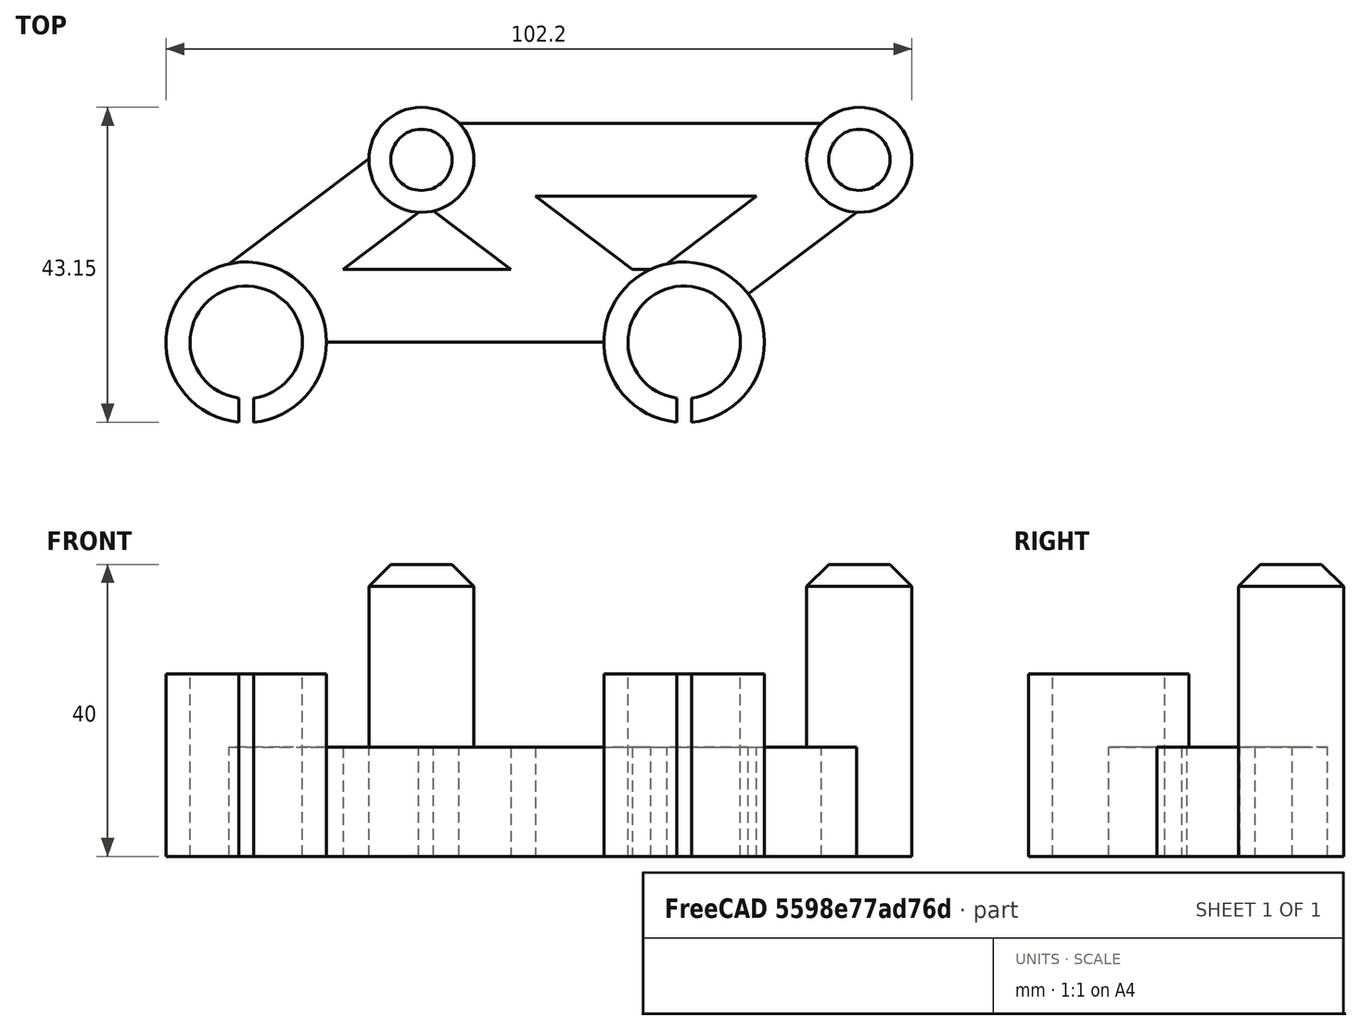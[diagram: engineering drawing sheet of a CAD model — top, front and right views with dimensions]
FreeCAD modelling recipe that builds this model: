
FCSTD DOCUMENT  (FreeCAD 0.17R13541 (Git))
Label: offset-rod-adaptor
License: All rights reserved
LicenseURL: http://en.wikipedia.org/wiki/All_rights_reserved
objects: Part::Box×7, Part::Cylinder×6, Part::Fuse×5, Part::Cut×4, Part::MultiFuse×2, Part::Chamfer×1
note: 25 computed .brp shape members not serialized (recipe doc carries the construction recipe); baked Part::Feature solids carry a one-line shape summary decoded from their .brp

FEATURE [Part::Cylinder] Cylinder
  Angle = 360
  AttacherType = Attacher::AttachEngine3D
  Height = 25
  Radius = 7.7
FEATURE [Part::Cylinder] Cylinder001
  Angle = 360
  AttacherType = Attacher::AttachEngine3D
  Height = 25
  Placement = pos=(60,0,0) rot=(0,0,1;0rad)
  Radius = 7.7
FEATURE [Part::Cylinder] Cylinder002
  Angle = 360
  AttacherType = Attacher::AttachEngine3D
  Height = 25
  Radius = 11
FEATURE [Part::Cylinder] Cylinder003
  Angle = 360
  AttacherType = Attacher::AttachEngine3D
  Height = 25
  Placement = pos=(60,0,0) rot=(0,0,1;0rad)
  Radius = 11
FEATURE [Part::Box] Box  label="Cube"
  AttacherType = Attacher::AttachEngine3D
  Height = 15
  Length = 60
  Width = 10
FEATURE [Part::MultiFuse] Fusion
  Shapes = -> [Cylinder003,Box,Cylinder002]
FEATURE [Part::Cylinder] Cylinder004
  Angle = 360
  AttacherType = Attacher::AttachEngine3D
  Height = 40
  Radius = 7.2
FEATURE [Part::Cylinder] Cylinder005
  Angle = 360
  AttacherType = Attacher::AttachEngine3D
  Height = 40
  Placement = pos=(60,0,0) rot=(0,0,1;0rad)
  Radius = 7.2
FEATURE [Part::Box] Box001  label="Cube001"
  AttacherType = Attacher::AttachEngine3D
  Height = 15
  Length = 60
  Placement = pos=(0,-5,0) rot=(0,0,1;0rad)
  Width = 10
FEATURE [Part::Fuse] Fusion001
  Base = -> Cylinder004
  Tool = -> Cylinder005
FEATURE [Part::Fuse] Fusion002
  Base = -> Box001
  Tool = -> Fusion001
FEATURE [Part::Chamfer] Chamfer
  Base = -> Fusion002
  Edges = 2 edges r=3: [Edge1,Edge21]
  Placement = pos=(24,25,0) rot=(0,0,1;0rad)
FEATURE [Part::Box] Box002  label="Cube002"
  AttacherType = Attacher::AttachEngine3D
  Height = 15
  Length = 34
  Placement = pos=(0,0,0) rot=(0,0,1;0.645772rad)
  Width = 10
FEATURE [Part::Box] Box003  label="Cube003"
  AttacherType = Attacher::AttachEngine3D
  Height = 15
  Length = 34
  Placement = pos=(60,0,0) rot=(0,0,1;0.645772rad)
  Width = 10
FEATURE [Part::Box] Box004  label="Cube004"
  AttacherType = Attacher::AttachEngine3D
  Height = 15
  Length = 32
  Placement = pos=(23,20,0) rot=(0,0,-1;0.645772rad)
  Width = 10
FEATURE [Part::Fuse] Fusion003
  Base = -> Fusion
  Tool = -> Box004
FEATURE [Part::Fuse] Fusion004
  Base = -> Box003
  Tool = -> Fusion003
FEATURE [Part::Fuse] Fusion005
  Base = -> Box002
  Tool = -> Fusion004
FEATURE [Part::Cut] Cut
  Base = -> Fusion005
  Tool = -> Cylinder
FEATURE [Part::Cut] Cut001
  Base = -> Cut
  Tool = -> Cylinder001
FEATURE [Part::Box] Box005  label="Cube005"
  AttacherType = Attacher::AttachEngine3D
  Height = 30
  Length = 2
  Placement = pos=(-1,-15,0) rot=(0,0,1;0rad)
  Width = 10
FEATURE [Part::Box] Box006  label="Cube006"
  AttacherType = Attacher::AttachEngine3D
  Height = 30
  Length = 2
  Placement = pos=(59,-15,0) rot=(0,0,1;0rad)
  Width = 10
FEATURE [Part::Cut] Cut002
  Base = -> Cut001
  Tool = -> Box005
FEATURE [Part::Cut] Cut003
  Base = -> Cut002
  Tool = -> Box006
FEATURE [Part::MultiFuse] Fusion006
  Shapes = -> [Chamfer,Cut003]
